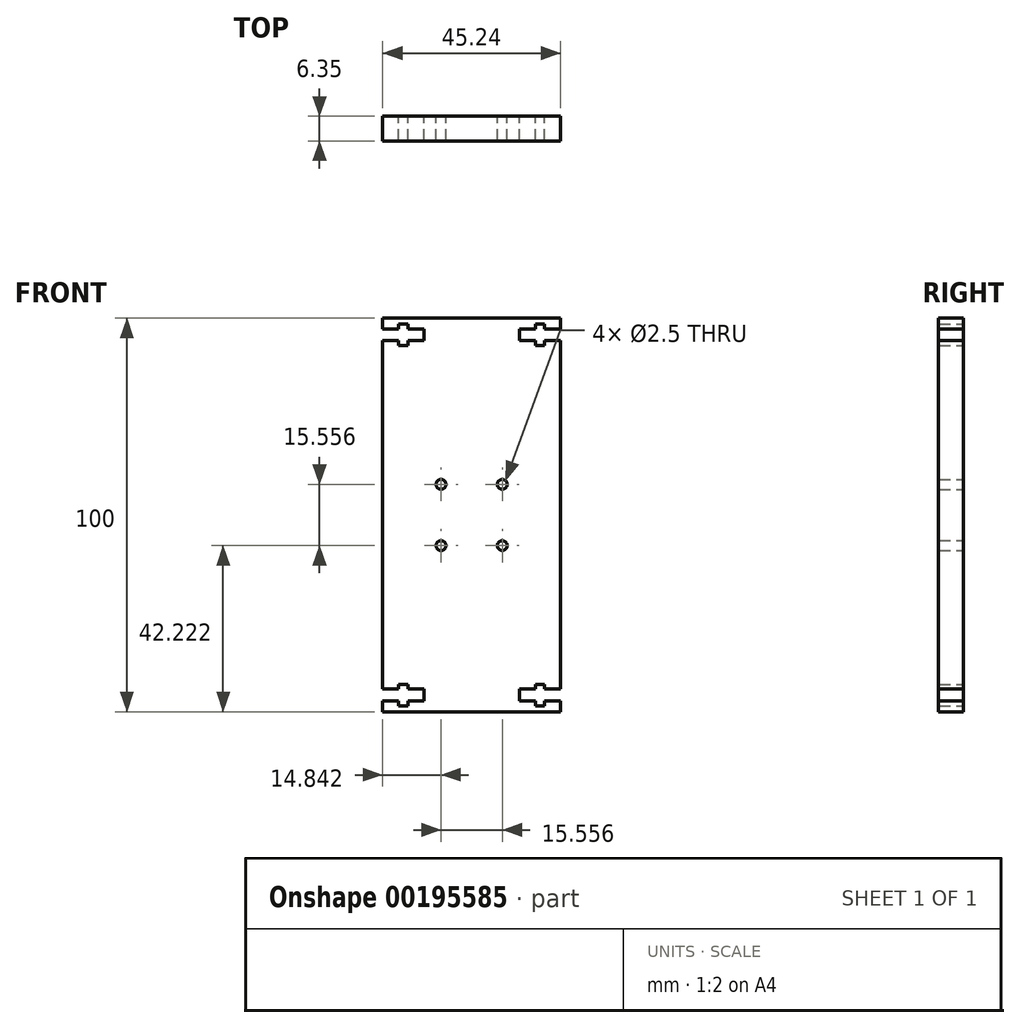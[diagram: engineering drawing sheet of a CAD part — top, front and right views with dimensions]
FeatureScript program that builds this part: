
annotation { "Feature Type Name" : "Feature", "Feature Type Description" : "" }
export const myFeature = defineFeature(function(context is Context, id is Id, definition is map)
    precondition{}
    {
        {
            var Q0;
            Q0=qCreatedBy(makeId("Front.planeOp"),FACE);
            var sketch = newSketch(context, id + "F0", { "sketchPlane" : qUnion([Q0])});
            skLineSegment(sketch, "E0.bottom", {"start": v(22.63, 50) * mm, "end": v(-22.63, 50) * mm});
            skLineSegment(sketch, "E0.top", {"start": v(22.62, -50) * mm, "end": v(-22.62, -50) * mm});
            skLineSegment(sketch, "E0.left", {"start": v(22.63, 50) * mm, "end": v(22.63, 47.26) * mm});
            skLineSegment(sketch, "E0.right", {"start": v(-22.62, 50) * mm, "end": v(-22.62, 47.26) * mm});
            skPoint(sketch, "E0.middle", {"position": v(0, 0) * mm});
            skLineSegment(sketch, "E1", {"start": v(-63, 0) * mm, "end": v(62.83, 0) * mm, "construction": true});
            skLineSegment(sketch, "E2", {"start": v(0, -40.7) * mm, "end": v(0, 40.67) * mm, "construction": true});
            skPoint(sketch, "E2.endSnap0", {"position": v(0, 50) * mm});
            skLineSegment(sketch, "E3", {"start": v(22.63, 47.26) * mm, "end": v(18.55, 47.26) * mm});
            skLineSegment(sketch, "E4", {"start": v(18.54, 47.26) * mm, "end": v(18.54, 48.46) * mm});
            skLineSegment(sketch, "E5", {"start": v(18.55, 48.46) * mm, "end": v(16.2, 48.46) * mm});
            skLineSegment(sketch, "E6", {"start": v(16.2, 48.46) * mm, "end": v(16.2, 47.26) * mm});
            skLineSegment(sketch, "E7", {"start": v(16.2, 47.26) * mm, "end": v(12.12, 47.26) * mm});
            skLineSegment(sketch, "E8", {"start": v(12.13, 47.26) * mm, "end": v(12.12, 44.26) * mm});
            skLineSegment(sketch, "E9", {"start": v(12.12, 44.26) * mm, "end": v(16.2, 44.26) * mm});
            skLineSegment(sketch, "E10", {"start": v(16.2, 44.26) * mm, "end": v(16.2, 43.06) * mm});
            skLineSegment(sketch, "E11", {"start": v(16.2, 43.05) * mm, "end": v(18.55, 43.05) * mm});
            skLineSegment(sketch, "E12", {"start": v(18.54, 43.06) * mm, "end": v(18.54, 44.26) * mm});
            skLineSegment(sketch, "E13", {"start": v(18.55, 44.26) * mm, "end": v(22.63, 44.26) * mm});
            skLineSegment(sketch, "E14", {"start": v(12.12, 45.76) * mm, "end": v(22.63, 45.76) * mm, "construction": true});
            skCircle(sketch, "E15", {"center": v(0, 0) * mm, "radius": 11 * mm, "construction": true});
            skCircle(sketch, "E16", {"center": v(7.78, 7.78) * mm, "radius": 1.25 * mm});
            skCircle(sketch, "E17", {"center": v(7.78, -7.78) * mm, "radius": 1.25 * mm});
            skCircle(sketch, "E18", {"center": v(-7.78, -7.78) * mm, "radius": 1.25 * mm});
            skCircle(sketch, "E19", {"center": v(-7.78, 7.78) * mm, "radius": 1.25 * mm});
            skLineSegment(sketch, "E20", {"start": v(-12.85, -12.85) * mm, "end": v(12.2, 12.2) * mm, "construction": true});
            skLineSegment(sketch, "E21", {"start": v(12.5, -12.5) * mm, "end": v(-13.53, 13.53) * mm, "construction": true});
            skLineSegment(sketch, "E22.trimOffspring", {"start": v(22.63, 44.26) * mm, "end": v(22.62, -44.26) * mm});
            skLineSegment(sketch, "E23.MirrorCS", {"start": v(22.63, -47.26) * mm, "end": v(18.55, -47.26) * mm});
            skLineSegment(sketch, "E24.MirrorCS", {"start": v(16.2, -44.26) * mm, "end": v(16.2, -43.06) * mm});
            skLineSegment(sketch, "E25.MirrorCS", {"start": v(18.54, -47.26) * mm, "end": v(18.54, -48.46) * mm});
            skLineSegment(sketch, "E26.MirrorCS", {"start": v(16.2, -48.46) * mm, "end": v(16.2, -47.26) * mm});
            skLineSegment(sketch, "E27.MirrorCS", {"start": v(18.54, -43.06) * mm, "end": v(18.54, -44.26) * mm});
            skLineSegment(sketch, "E28.MirrorCS", {"start": v(12.12, -47.26) * mm, "end": v(12.12, -44.26) * mm});
            skLineSegment(sketch, "E29.MirrorCS", {"start": v(18.55, -44.26) * mm, "end": v(22.63, -44.26) * mm});
            skLineSegment(sketch, "E30.MirrorCS", {"start": v(12.12, -44.26) * mm, "end": v(16.2, -44.26) * mm});
            skLineSegment(sketch, "E31.MirrorCS", {"start": v(16.2, -47.26) * mm, "end": v(12.12, -47.26) * mm});
            skLineSegment(sketch, "E32.MirrorCS", {"start": v(18.55, -48.46) * mm, "end": v(16.2, -48.46) * mm});
            skLineSegment(sketch, "E33.MirrorCS", {"start": v(16.2, -43.05) * mm, "end": v(18.55, -43.05) * mm});
            skLineSegment(sketch, "E34.MirrorCS", {"start": v(12.12, -45.76) * mm, "end": v(22.63, -45.76) * mm, "construction": true});
            skLineSegment(sketch, "E35.trimOffspring", {"start": v(22.62, -47.26) * mm, "end": v(22.62, -50) * mm});
            skLineSegment(sketch, "E36.MirrorCS", {"start": v(-18.55, -48.46) * mm, "end": v(-16.2, -48.46) * mm});
            skLineSegment(sketch, "E37.MirrorCS", {"start": v(-18.54, -47.26) * mm, "end": v(-18.54, -48.46) * mm});
            skLineSegment(sketch, "E38.MirrorCS", {"start": v(-18.54, -43.06) * mm, "end": v(-18.54, -44.26) * mm});
            skLineSegment(sketch, "E39.MirrorCS", {"start": v(-16.2, -43.05) * mm, "end": v(-18.55, -43.05) * mm});
            skLineSegment(sketch, "E40.MirrorCS", {"start": v(-16.2, -48.46) * mm, "end": v(-16.2, -47.26) * mm});
            skLineSegment(sketch, "E41.MirrorCS", {"start": v(-16.2, -44.26) * mm, "end": v(-16.2, -43.06) * mm});
            skLineSegment(sketch, "E42.MirrorCS", {"start": v(-22.63, -47.26) * mm, "end": v(-18.55, -47.26) * mm});
            skLineSegment(sketch, "E43.MirrorCS", {"start": v(-12.12, -47.26) * mm, "end": v(-12.12, -44.26) * mm});
            skLineSegment(sketch, "E44.MirrorCS", {"start": v(-16.2, -47.26) * mm, "end": v(-12.13, -47.26) * mm});
            skLineSegment(sketch, "E45.MirrorCS", {"start": v(-12.12, -45.76) * mm, "end": v(-22.63, -45.76) * mm, "construction": true});
            skLineSegment(sketch, "E46.MirrorCS", {"start": v(-12.12, -44.26) * mm, "end": v(-16.2, -44.26) * mm});
            skLineSegment(sketch, "E47.MirrorCS", {"start": v(-18.55, -44.26) * mm, "end": v(-22.63, -44.26) * mm});
            skLineSegment(sketch, "E48.MirrorCS", {"start": v(-22.63, 47.26) * mm, "end": v(-18.55, 47.26) * mm});
            skLineSegment(sketch, "E49.MirrorCS", {"start": v(-12.13, 47.26) * mm, "end": v(-12.12, 44.26) * mm});
            skLineSegment(sketch, "E50.MirrorCS", {"start": v(-16.2, 47.26) * mm, "end": v(-12.13, 47.26) * mm});
            skLineSegment(sketch, "E51.MirrorCS", {"start": v(-18.55, 44.26) * mm, "end": v(-22.63, 44.26) * mm});
            skLineSegment(sketch, "E52.MirrorCS", {"start": v(-16.2, 44.26) * mm, "end": v(-16.2, 43.06) * mm});
            skLineSegment(sketch, "E53.MirrorCS", {"start": v(-12.12, 45.76) * mm, "end": v(-22.63, 45.76) * mm, "construction": true});
            skLineSegment(sketch, "E54.MirrorCS", {"start": v(-16.2, 43.05) * mm, "end": v(-18.55, 43.05) * mm});
            skLineSegment(sketch, "E55.MirrorCS", {"start": v(-18.55, 43.06) * mm, "end": v(-18.55, 44.26) * mm});
            skLineSegment(sketch, "E56.MirrorCS", {"start": v(-16.2, 48.46) * mm, "end": v(-16.2, 47.26) * mm});
            skLineSegment(sketch, "E57.MirrorCS", {"start": v(-18.55, 48.46) * mm, "end": v(-16.2, 48.46) * mm});
            skLineSegment(sketch, "E58.MirrorCS", {"start": v(-18.54, 47.26) * mm, "end": v(-18.54, 48.46) * mm});
            skLineSegment(sketch, "E59.MirrorCS", {"start": v(-12.13, 44.26) * mm, "end": v(-16.2, 44.26) * mm});
            skLineSegment(sketch, "E60.trimOffspring", {"start": v(-22.62, 44.26) * mm, "end": v(-22.63, -44.26) * mm});
            skLineSegment(sketch, "E61.trimOffspring", {"start": v(-22.63, -47.26) * mm, "end": v(-22.63, -50) * mm});
            skSolve(sketch);
        }
        {
            var Q0;
            Q0=makeQuery(id+"F0.imprint","IMPRINT",FACE,{"disambiguationData":[TD([[makeQuery(id+"F0.imprint","IMPRINT",EDGE,{"derivedFrom":sQuery(id+"F0.wireOp",EDGE,"E0.bottom")}),1.0]])]});
            extrude(context, id + "F1", {"entities" : qUnion([Q0]), "depth" : 6.35 * mm});
        }
    });
